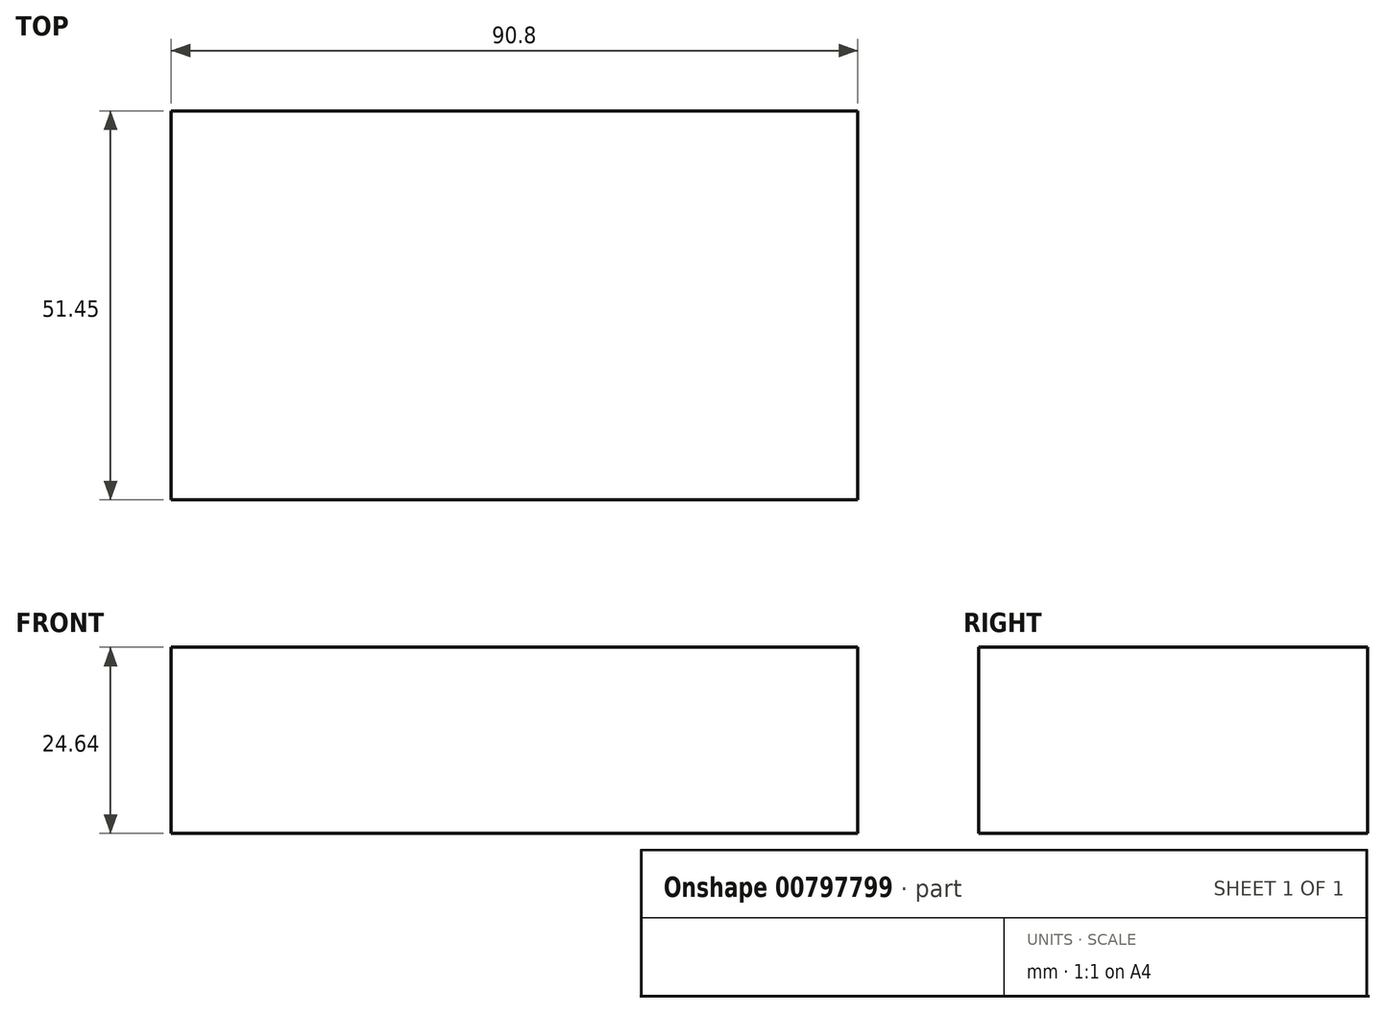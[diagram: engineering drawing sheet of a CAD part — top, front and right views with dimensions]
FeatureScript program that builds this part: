
annotation { "Feature Type Name" : "Feature", "Feature Type Description" : "" }
export const myFeature = defineFeature(function(context is Context, id is Id, definition is map)
    precondition{}
    {
        {
            var Q0;
            Q0=qCreatedBy(makeId("Top.planeOp"),FACE);
            var sketch = newSketch(context, id + "F0", { "sketchPlane" : qUnion([Q0])});
            skLineSegment(sketch, "E0.bottom", {"start": v(-44.35, 8.36) * mm, "end": v(46.45, 8.36) * mm});
            skLineSegment(sketch, "E0.top", {"start": v(-44.35, -43.09) * mm, "end": v(46.45, -43.09) * mm});
            skLineSegment(sketch, "E0.left", {"start": v(-44.35, 8.36) * mm, "end": v(-44.35, -43.09) * mm});
            skLineSegment(sketch, "E0.right", {"start": v(46.45, 8.36) * mm, "end": v(46.45, -43.09) * mm});
            skSolve(sketch);
        }
        {
            var Q0;
            Q0=makeQuery(id+"F0.imprint","IMPRINT",FACE,{"disambiguationData":[TD([[makeQuery(id+"F0.imprint","IMPRINT",EDGE,{"derivedFrom":sQuery(id+"F0.wireOp",EDGE,"E0.bottom")}),-1.0]])]});
            extrude(context, id + "F1", {"entities" : qUnion([Q0]), "depth" : 24.64 * mm, "offsetDistance" : 25.4 * mm});
        }
    });
